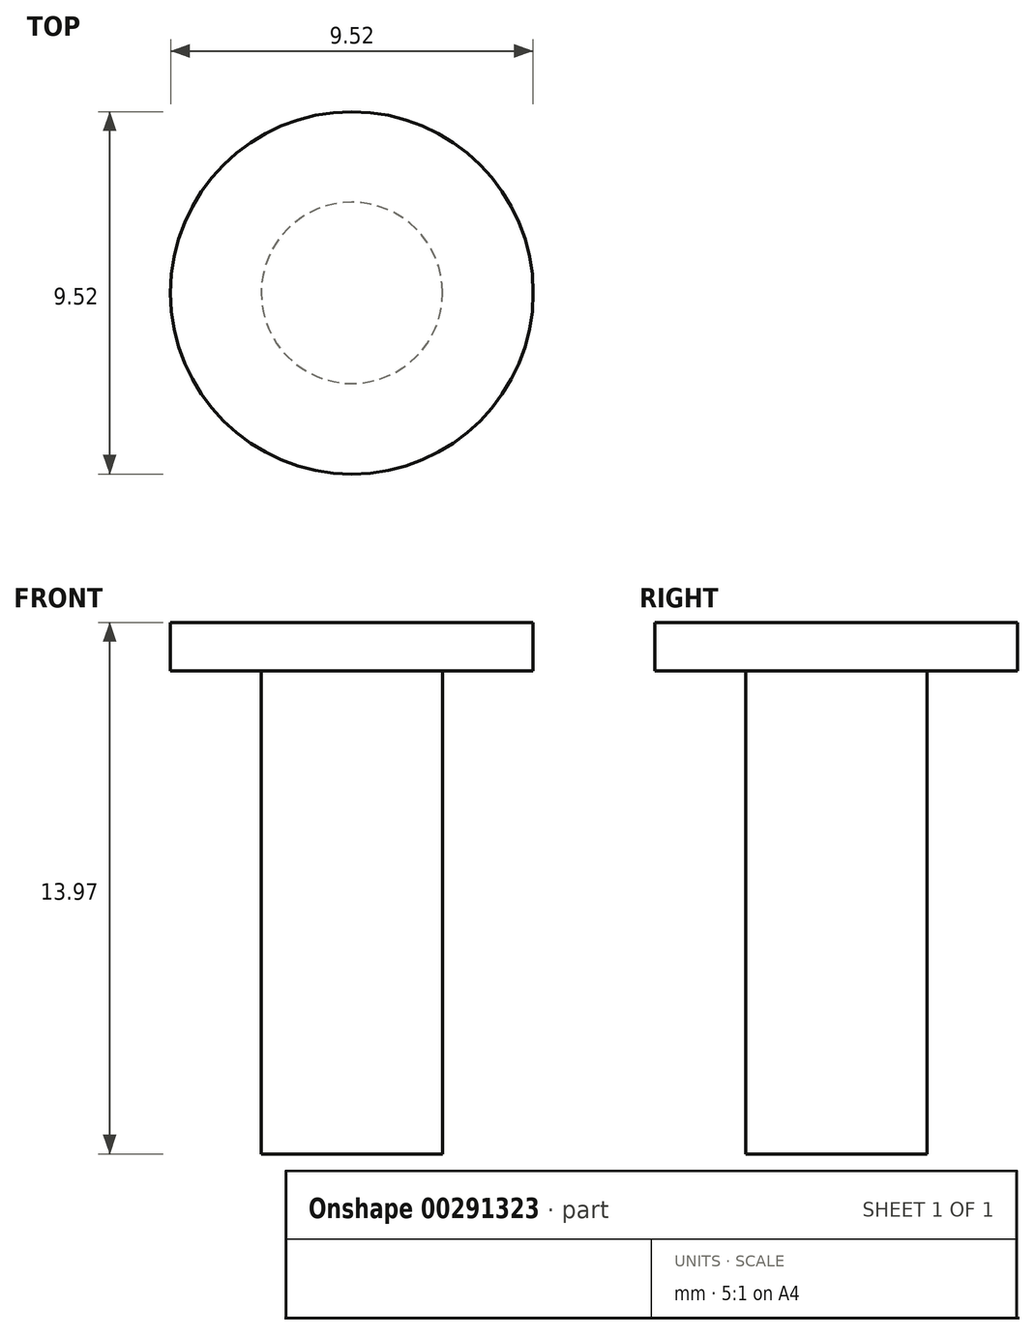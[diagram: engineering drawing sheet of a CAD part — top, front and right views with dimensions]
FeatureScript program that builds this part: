
annotation { "Feature Type Name" : "Feature", "Feature Type Description" : "" }
export const myFeature = defineFeature(function(context is Context, id is Id, definition is map)
    precondition{}
    {
        {
            var Q0;
            Q0=qCreatedBy(makeId("Right.planeOp"),FACE);
            var sketch = newSketch(context, id + "F0", { "sketchPlane" : qUnion([Q0])});
            skLineSegment(sketch, "E0", {"start": v(0, 12.25) * mm, "end": v(4.76, 12.25) * mm});
            skLineSegment(sketch, "E1", {"start": v(4.76, 12.25) * mm, "end": v(4.76, 10.98) * mm});
            skLineSegment(sketch, "E2", {"start": v(4.76, 10.98) * mm, "end": v(2.38, 10.98) * mm});
            skLineSegment(sketch, "E3", {"start": v(2.38, 10.98) * mm, "end": v(2.38, -1.72) * mm});
            skLineSegment(sketch, "E4", {"start": v(2.38, -1.72) * mm, "end": v(0, -1.72) * mm});
            skLineSegment(sketch, "E5", {"start": v(0, -1.72) * mm, "end": v(0, 12.25) * mm});
            skSolve(sketch);
        }
        {
            var Q0;
            Q0=makeQuery(id+"F0.imprint","IMPRINT",FACE,{"disambiguationData":[TD([[makeQuery(id+"F0.imprint","IMPRINT",EDGE,{"derivedFrom":sQuery(id+"F0.wireOp",EDGE,"E0")}),-1.0]])]});
            var Q1;
            Q1=sQuery(id+"F0.wireOp",EDGE,"E5");
            revolve(context, id + "F1", {"entities" : qUnion([Q0]), "axis" : qUnion([Q1]), "revolveType" : RevolveType.FULL});
        }
    });
